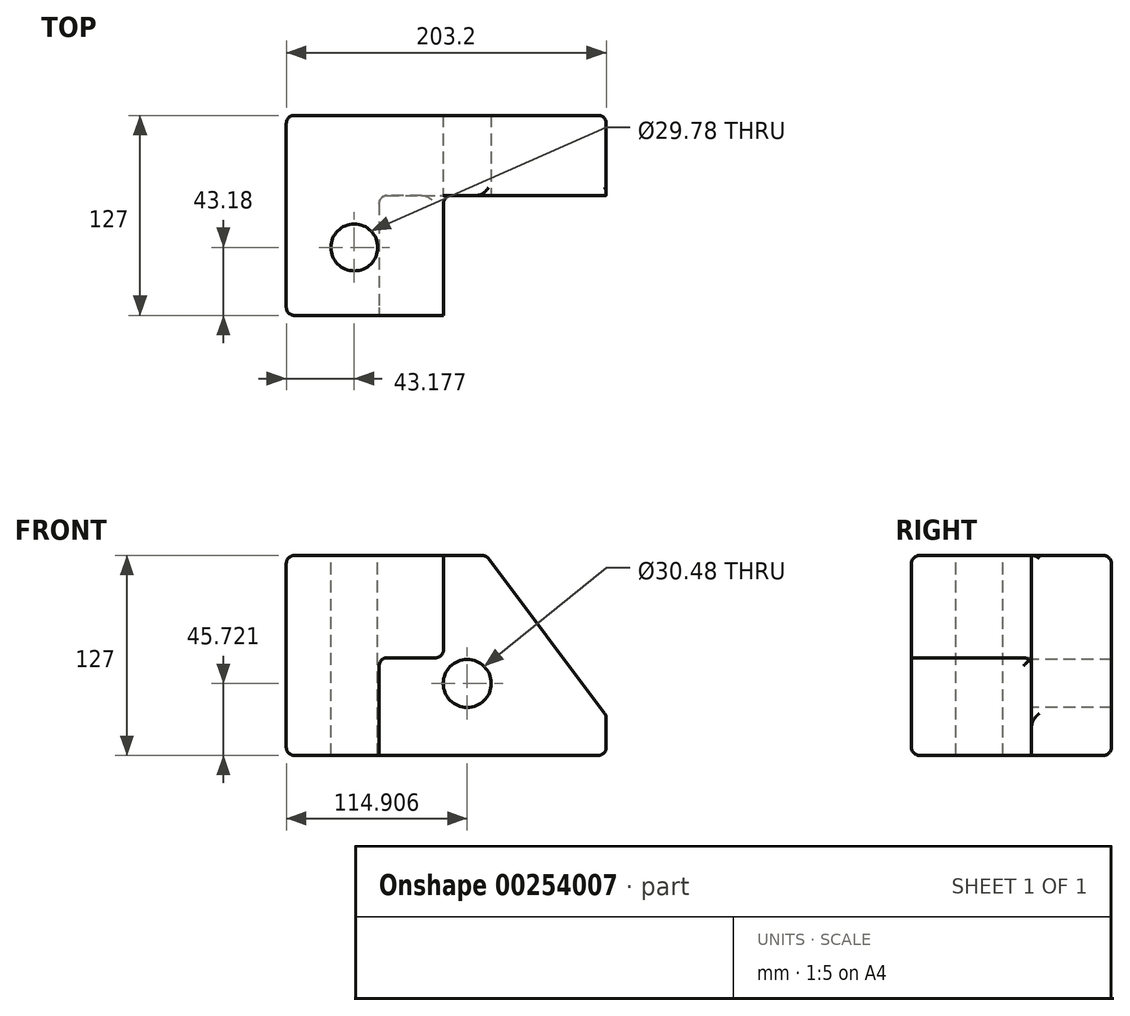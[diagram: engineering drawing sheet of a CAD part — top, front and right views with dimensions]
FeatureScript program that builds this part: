
annotation { "Feature Type Name" : "Feature", "Feature Type Description" : "" }
export const myFeature = defineFeature(function(context is Context, id is Id, definition is map)
    precondition{}
    {
        {
            var Q0;
            Q0=qCreatedBy(makeId("Front.planeOp"),FACE);
            var sketch = newSketch(context, id + "F0", { "sketchPlane" : qUnion([Q0])});
            skLineSegment(sketch, "E0.bottom", {"start": v(-99.86, 64.96) * mm, "end": v(103.34, 64.96) * mm});
            skLineSegment(sketch, "E0.top", {"start": v(-99.86, -62.04) * mm, "end": v(103.34, -62.04) * mm});
            skLineSegment(sketch, "E0.left", {"start": v(-99.86, 64.96) * mm, "end": v(-99.86, -62.04) * mm});
            skLineSegment(sketch, "E0.right", {"start": v(103.34, 64.96) * mm, "end": v(103.34, -62.04) * mm});
            skSolve(sketch);
        }
        {
            var Q0;
            Q0 = qSketchRegion(id + "F0", true);
            extrude(context, id + "F1", {"entities" : qUnion([Q0]), "depth" : 127 * mm});
        }
        {
            var Q0;
            Q0=makeQuery(id+"F1.opExtrude","CAP_FACE",FACE,{"disambiguationData":[OSD([sQuery(id+"F0.wireOp",EDGE,"E0.bottom"),sQuery(id+"F0.wireOp",EDGE,"E0.top"),sQuery(id+"F0.wireOp",EDGE,"E0.left"),sQuery(id+"F0.wireOp",EDGE,"E0.right")])],"isStart":false});
            var sketch = newSketch(context, id + "F2", { "sketchPlane" : qUnion([Q0])});
            skLineSegment(sketch, "E1", {"start": v(0, 0) * mm, "end": v(0, 64.96) * mm});
            skLineSegment(sketch, "E2", {"start": v(0, 0) * mm, "end": v(-40.83, 0) * mm});
            skLineSegment(sketch, "E3", {"start": v(-40.83, 0) * mm, "end": v(-40.83, -62.04) * mm});
            skSolve(sketch);
        }
        {
            var Q0;
            {var subQ2=sQuery(id+"F2.wireOp",EDGE,"E1");Q0=makeQuery(id+"F2.imprint","IMPRINT",FACE,{"disambiguationData":[TD([[makeQuery(id+"F2.imprint","IMPRINT",EDGE,{"derivedFrom":subQ2}),-1.0]])]});}
            extrude(context, id + "F3", {"entities" : qUnion([Q0]), "operationType" : NewBodyOperationType.REMOVE, "oppositeDirection" : true, "depth" : 76.2 * mm});
        }
        {
            var Q0;
            Q0=makeQuery(id+"F1.opExtrude","SWEPT_EDGE",EDGE,{"disambiguationData":[OSD([sQuery(id+"F0.wireOp",EDGE,"E0.bottom"),sQuery(id+"F0.wireOp",EDGE,"E0.right")])]});
            chamfer(context, id + "F4", {"entities" : qUnion([Q0]), "chamferType" : ChamferType.TWO_OFFSETS, "width1" : 76.2 * mm, "oppositeDirection" : false, "width2" : 101.6 * mm, "tangentPropagation" : true});
        }
        {
            var Q0;
            Q0=makeQuery(id+"F1.opExtrude","SWEPT_EDGE",EDGE,{"disambiguationData":[OSD([sQuery(id+"F0.wireOp",EDGE,"E0.bottom"),sQuery(id+"F0.wireOp",EDGE,"E0.left")])]});
            var Q1;
            Q1=makeQuery(id+"F1.opExtrude","CAP_EDGE",EDGE,{"disambiguationData":[OSD([sQuery(id+"F0.wireOp",EDGE,"E0.bottom")])],"isStart":false});
            var Q2;
            Q2=makeQuery(id+"F3.boolean.opBoolean","COPY",EDGE,{"derivedFrom":makeQuery(id+"F3.opExtrude","SWEPT_EDGE",EDGE,{"disambiguationData":[OSD([sQuery(id+"F0.wireOp",EDGE,"E0.bottom"),sQuery(id+"F2.wireOp",EDGE,"E1")])]})});
            var Q3;
            {var subQ0=sQuery(id+"F0.wireOp",EDGE,"E0.bottom");Q3=makeQuery(id+"F4.opChamfer","BLEND_EDGE",EDGE,{"blendedFrom":[makeQuery(id+"F1.opExtrude","SWEPT_EDGE",EDGE,{"disambiguationData":[OSD([subQ0,sQuery(id+"F0.wireOp",EDGE,"E0.right")])]}),makeQuery(id+"F1.opExtrude","SWEPT_FACE",FACE,{"disambiguationData":[OSD([subQ0])]})],"blendedInto":[makeQuery(id+"F1.opExtrude","SWEPT_FACE",FACE,{"disambiguationData":[OSD([subQ0])]})]});}
            var Q4;
            Q4=makeQuery(id+"F3.boolean.opBoolean","COPY",EDGE,{"derivedFrom":makeQuery(id+"F3.opExtrude","CAP_EDGE",EDGE,{"disambiguationData":[OSD([sQuery(id+"F0.wireOp",EDGE,"E0.bottom")])],"isStart":false})});
            var Q5;
            {var subQ0=sQuery(id+"F0.wireOp",EDGE,"E0.right");var subQ1=sQuery(id+"F0.wireOp",EDGE,"E0.bottom");Q5=makeQuery(id+"F4.opChamfer","BLEND_EDGE",EDGE,{"blendedFrom":[makeQuery(id+"F1.opExtrude","SWEPT_EDGE",EDGE,{"disambiguationData":[OSD([subQ1,subQ0])]}),makeQuery(id+"F3.boolean.opBoolean","COPY",FACE,{"derivedFrom":makeQuery(id+"F3.opExtrude","CAP_FACE",FACE,{"disambiguationData":[OSD([subQ1,sQuery(id+"F0.wireOp",EDGE,"E0.top"),subQ0,sQuery(id+"F2.wireOp",EDGE,"E1"),sQuery(id+"F2.wireOp",EDGE,"E2"),sQuery(id+"F2.wireOp",EDGE,"E3")])],"isStart":false})})],"blendedInto":[makeQuery(id+"F3.boolean.opBoolean","COPY",FACE,{"derivedFrom":makeQuery(id+"F3.opExtrude","CAP_FACE",FACE,{"disambiguationData":[OSD([subQ1,sQuery(id+"F0.wireOp",EDGE,"E0.top"),subQ0,sQuery(id+"F2.wireOp",EDGE,"E1"),sQuery(id+"F2.wireOp",EDGE,"E2"),sQuery(id+"F2.wireOp",EDGE,"E3")])],"isStart":false})})]});}
            var Q6;
            Q6=makeQuery(id+"F3.boolean.opBoolean","COPY",EDGE,{"derivedFrom":makeQuery(id+"F3.opExtrude","CAP_EDGE",EDGE,{"disambiguationData":[OSD([sQuery(id+"F2.wireOp",EDGE,"E1")])],"isStart":false})});
            var Q7;
            Q7=makeQuery(id+"F3.boolean.opBoolean","COPY",EDGE,{"derivedFrom":makeQuery(id+"F3.opExtrude","CAP_EDGE",EDGE,{"disambiguationData":[OSD([sQuery(id+"F2.wireOp",EDGE,"E1")])],"isStart":true})});
            var Q8;
            Q8=makeQuery(id+"F3.boolean.opBoolean","COPY",EDGE,{"derivedFrom":makeQuery(id+"F3.opExtrude","CAP_EDGE",EDGE,{"disambiguationData":[OSD([sQuery(id+"F0.wireOp",EDGE,"E0.top")])],"isStart":false})});
            var Q9;
            Q9=makeQuery(id+"F3.boolean.opBoolean","COPY",EDGE,{"derivedFrom":makeQuery(id+"F3.opExtrude","CAP_EDGE",EDGE,{"disambiguationData":[OSD([sQuery(id+"F0.wireOp",EDGE,"E0.right")])],"isStart":false})});
            var Q10;
            {var subQ0=sQuery(id+"F0.wireOp",EDGE,"E0.right");Q10=makeQuery(id+"F4.opChamfer","BLEND_EDGE",EDGE,{"blendedFrom":[makeQuery(id+"F1.opExtrude","SWEPT_EDGE",EDGE,{"disambiguationData":[OSD([sQuery(id+"F0.wireOp",EDGE,"E0.bottom"),subQ0])]}),makeQuery(id+"F1.opExtrude","SWEPT_FACE",FACE,{"disambiguationData":[OSD([subQ0])]})],"blendedInto":[makeQuery(id+"F1.opExtrude","SWEPT_FACE",FACE,{"disambiguationData":[OSD([subQ0])]})]});}
            var Q11;
            Q11=makeQuery(id+"F1.opExtrude","SWEPT_EDGE",EDGE,{"disambiguationData":[OSD([sQuery(id+"F0.wireOp",EDGE,"E0.top"),sQuery(id+"F0.wireOp",EDGE,"E0.right")])]});
            var Q12;
            Q12=makeQuery(id+"F1.opExtrude","CAP_EDGE",EDGE,{"disambiguationData":[OSD([sQuery(id+"F0.wireOp",EDGE,"E0.right")])],"isStart":true});
            var Q13;
            {var subQ0=sQuery(id+"F0.wireOp",EDGE,"E0.right");var subQ1=sQuery(id+"F0.wireOp",EDGE,"E0.bottom");Q13=makeQuery(id+"F4.opChamfer","BLEND_EDGE",EDGE,{"blendedFrom":[makeQuery(id+"F1.opExtrude","SWEPT_EDGE",EDGE,{"disambiguationData":[OSD([subQ1,subQ0])]}),makeQuery(id+"F1.opExtrude","CAP_FACE",FACE,{"disambiguationData":[OSD([subQ1,sQuery(id+"F0.wireOp",EDGE,"E0.top"),sQuery(id+"F0.wireOp",EDGE,"E0.left"),subQ0])],"isStart":true})],"blendedInto":[makeQuery(id+"F1.opExtrude","CAP_FACE",FACE,{"disambiguationData":[OSD([subQ1,sQuery(id+"F0.wireOp",EDGE,"E0.top"),sQuery(id+"F0.wireOp",EDGE,"E0.left"),subQ0])],"isStart":true})]});}
            var Q14;
            Q14=makeQuery(id+"F3.boolean.opBoolean","COPY",EDGE,{"derivedFrom":makeQuery(id+"F3.opExtrude","CAP_EDGE",EDGE,{"disambiguationData":[OSD([sQuery(id+"F2.wireOp",EDGE,"E2")])],"isStart":true})});
            var Q15;
            Q15=makeQuery(id+"F3.boolean.opBoolean","COPY",EDGE,{"derivedFrom":makeQuery(id+"F3.opExtrude","CAP_EDGE",EDGE,{"disambiguationData":[OSD([sQuery(id+"F2.wireOp",EDGE,"E3")])],"isStart":true})});
            var Q16;
            Q16=makeQuery(id+"F3.boolean.opBoolean","COPY",EDGE,{"derivedFrom":makeQuery(id+"F3.opExtrude","SWEPT_EDGE",EDGE,{"disambiguationData":[OSD([sQuery(id+"F0.wireOp",EDGE,"E0.top"),sQuery(id+"F2.wireOp",EDGE,"E3")])]})});
            var Q17;
            Q17=makeQuery(id+"F3.boolean.opBoolean","COPY",EDGE,{"derivedFrom":makeQuery(id+"F3.opExtrude","CAP_EDGE",EDGE,{"disambiguationData":[OSD([sQuery(id+"F2.wireOp",EDGE,"E3")])],"isStart":false})});
            var Q18;
            Q18=makeQuery(id+"F3.boolean.opBoolean","COPY",EDGE,{"derivedFrom":makeQuery(id+"F3.opExtrude","SWEPT_EDGE",EDGE,{"disambiguationData":[OSD([sQuery(id+"F2.wireOp",EDGE,"E1"),sQuery(id+"F2.wireOp",EDGE,"E2")])]})});
            var Q19;
            Q19=makeQuery(id+"F3.boolean.opBoolean","COPY",EDGE,{"derivedFrom":makeQuery(id+"F3.opExtrude","SWEPT_EDGE",EDGE,{"disambiguationData":[OSD([sQuery(id+"F2.wireOp",EDGE,"E2"),sQuery(id+"F2.wireOp",EDGE,"E3")])]})});
            var Q20;
            Q20=makeQuery(id+"F1.opExtrude","SWEPT_EDGE",EDGE,{"disambiguationData":[OSD([sQuery(id+"F0.wireOp",EDGE,"E0.top"),sQuery(id+"F0.wireOp",EDGE,"E0.left")])]});
            var Q21;
            Q21=makeQuery(id+"F1.opExtrude","CAP_EDGE",EDGE,{"disambiguationData":[OSD([sQuery(id+"F0.wireOp",EDGE,"E0.top")])],"isStart":false});
            var Q22;
            Q22=makeQuery(id+"F1.opExtrude","CAP_EDGE",EDGE,{"disambiguationData":[OSD([sQuery(id+"F0.wireOp",EDGE,"E0.top")])],"isStart":true});
            var Q23;
            Q23=makeQuery(id+"F1.opExtrude","CAP_EDGE",EDGE,{"disambiguationData":[OSD([sQuery(id+"F0.wireOp",EDGE,"E0.left")])],"isStart":false});
            var Q24;
            Q24=makeQuery(id+"F1.opExtrude","CAP_EDGE",EDGE,{"disambiguationData":[OSD([sQuery(id+"F0.wireOp",EDGE,"E0.left")])],"isStart":true});
            var Q25;
            Q25=makeQuery(id+"F1.opExtrude","CAP_EDGE",EDGE,{"disambiguationData":[OSD([sQuery(id+"F0.wireOp",EDGE,"E0.bottom")])],"isStart":true});
            fillet(context, id + "F5", {"entities" : qUnion([Q0, Q1, Q2, Q3, Q4, Q5, Q6, Q7, Q8, Q9, Q10, Q11, Q12, Q13, Q14, Q15, Q16, Q17, Q18, Q19, Q20, Q21, Q22, Q23, Q24, Q25]), "radius" : 5.08 * mm, "tangentPropagation" : true, "allowEdgeOverflow" : false});
        }
        {
            var Q0;
            Q0=makeQuery(id+"F3.boolean.opBoolean","COPY",FACE,{"derivedFrom":makeQuery(id+"F3.opExtrude","CAP_FACE",FACE,{"disambiguationData":[OSD([sQuery(id+"F0.wireOp",EDGE,"E0.bottom"),sQuery(id+"F0.wireOp",EDGE,"E0.top"),sQuery(id+"F0.wireOp",EDGE,"E0.right"),sQuery(id+"F2.wireOp",EDGE,"E1"),sQuery(id+"F2.wireOp",EDGE,"E2"),sQuery(id+"F2.wireOp",EDGE,"E3")])],"isStart":false})});
            var sketch = newSketch(context, id + "F6", { "sketchPlane" : qUnion([Q0])});
            skCircle(sketch, "E4", {"center": v(15.05, -16.32) * mm, "radius": 15.24 * mm});
            skSolve(sketch);
        }
        {
            var Q0;
            Q0=makeQuery(id+"F6.imprint","IMPRINT",FACE,{"disambiguationData":[TD([[makeQuery(id+"F6.imprint","IMPRINT",EDGE,{"derivedFrom":sQuery(id+"F6.wireOp",EDGE,"E4")}),1.0]])]});
            var Q1;
            Q1=makeQuery(id+"F1.opExtrude","CAP_FACE",FACE,{"disambiguationData":[OSD([sQuery(id+"F0.wireOp",EDGE,"E0.bottom"),sQuery(id+"F0.wireOp",EDGE,"E0.top"),sQuery(id+"F0.wireOp",EDGE,"E0.left"),sQuery(id+"F0.wireOp",EDGE,"E0.right")])],"isStart":true});
            extrude(context, id + "F7", {"entities" : qUnion([Q0]), "operationType" : NewBodyOperationType.REMOVE, "endBound" : BoundingType.UP_TO_SURFACE, "oppositeDirection" : true, "endBoundEntityFace" : qUnion([Q1]), "depth" : 25.4 * mm});
        }
        {
            var Q0;
            Q0=makeQuery(id+"F1.opExtrude","SWEPT_FACE",FACE,{"disambiguationData":[OSD([sQuery(id+"F0.wireOp",EDGE,"E0.bottom")])]});
            var sketch = newSketch(context, id + "F8", { "sketchPlane" : qUnion([Q0])});
            skCircle(sketch, "E5", {"center": v(-56.68, -83.82) * mm, "radius": 14.9 * mm});
            skSolve(sketch);
        }
        {
            var Q0;
            Q0=makeQuery(id+"F8.imprint","IMPRINT",FACE,{"disambiguationData":[TD([[makeQuery(id+"F8.imprint","IMPRINT",EDGE,{"derivedFrom":sQuery(id+"F8.wireOp",EDGE,"E5")}),1.0]])]});
            var Q1;
            Q1=makeQuery(id+"F1.opExtrude","SWEPT_FACE",FACE,{"disambiguationData":[OSD([sQuery(id+"F0.wireOp",EDGE,"E0.top")])]});
            extrude(context, id + "F9", {"entities" : qUnion([Q0]), "operationType" : NewBodyOperationType.REMOVE, "endBound" : BoundingType.UP_TO_SURFACE, "oppositeDirection" : true, "endBoundEntityFace" : qUnion([Q1]), "depth" : 25.4 * mm});
        }
    });
